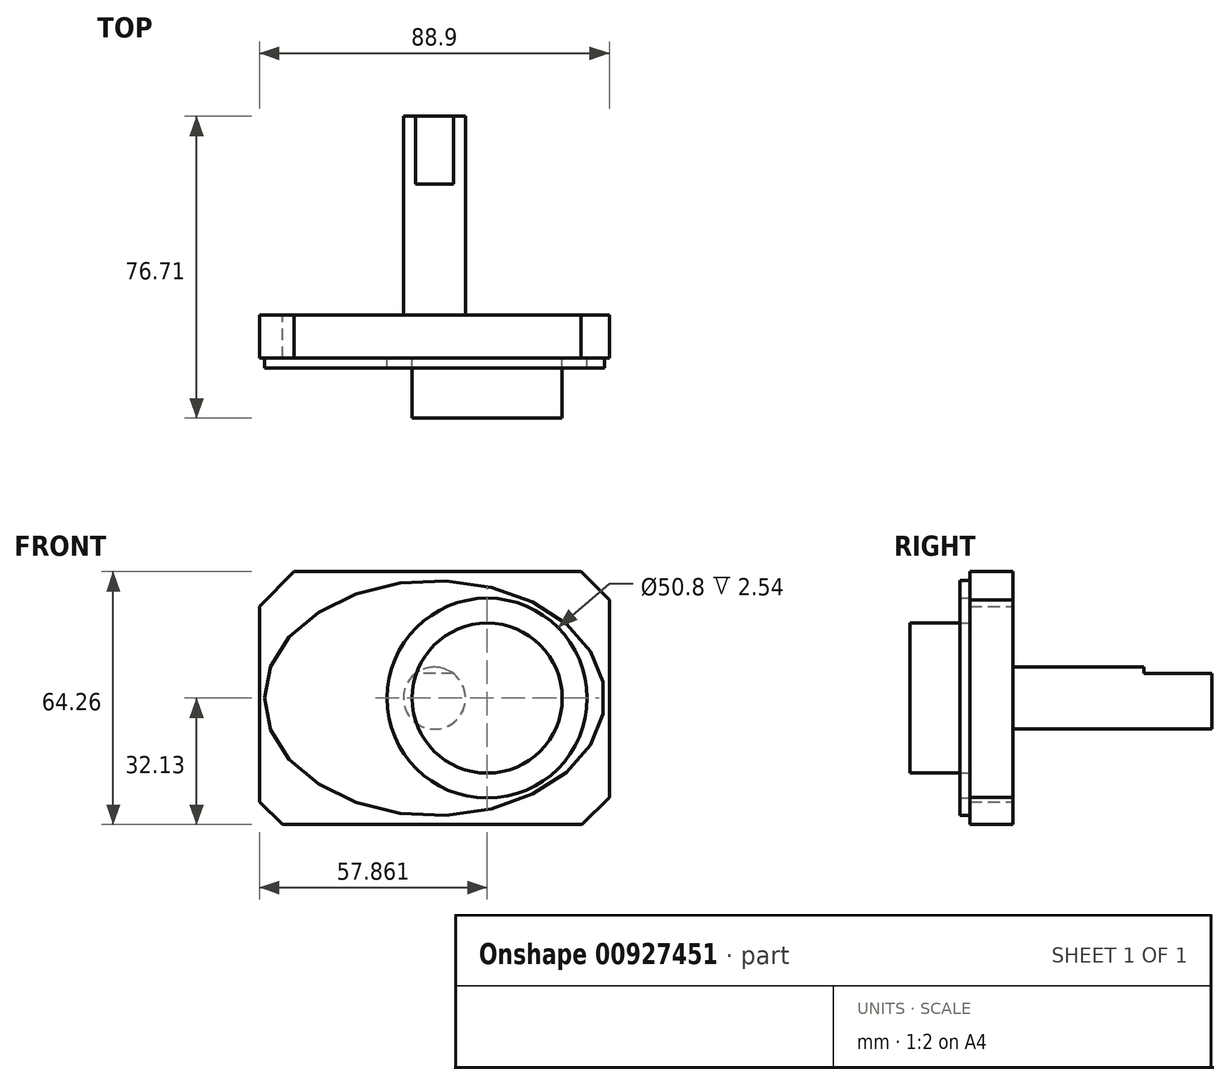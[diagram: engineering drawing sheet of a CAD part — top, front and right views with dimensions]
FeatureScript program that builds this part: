
annotation { "Feature Type Name" : "Feature", "Feature Type Description" : "" }
export const myFeature = defineFeature(function(context is Context, id is Id, definition is map)
    precondition{}
    {
        {
            var Q0;
            Q0=qCreatedBy(makeId("Front.planeOp"),FACE);
            var sketch = newSketch(context, id + "F0", { "sketchPlane" : qUnion([Q0])});
            skLineSegment(sketch, "E0.bottom", {"start": v(-44.45, -32.13) * mm, "end": v(44.45, -32.13) * mm});
            skLineSegment(sketch, "E0.top", {"start": v(-44.45, 32.13) * mm, "end": v(44.45, 32.13) * mm});
            skLineSegment(sketch, "E0.left", {"start": v(-44.45, -32.13) * mm, "end": v(-44.45, 32.13) * mm});
            skLineSegment(sketch, "E0.right", {"start": v(44.45, -32.13) * mm, "end": v(44.45, 32.13) * mm});
            skLineSegment(sketch, "E1", {"start": v(-44.45, 23.33) * mm, "end": v(-35.65, 32.13) * mm});
            skLineSegment(sketch, "E2", {"start": v(37.25, 32.13) * mm, "end": v(44.45, 24.93) * mm});
            skLineSegment(sketch, "E3", {"start": v(44.45, -25.16) * mm, "end": v(37.48, -32.13) * mm});
            skLineSegment(sketch, "E4", {"start": v(-44.45, -26.31) * mm, "end": v(-38.63, -32.13) * mm});
            skSolve(sketch);
        }
        {
            var Q0;
            {var subQ3=sQuery(id+"F0.wireOp",EDGE,"E1");Q0=makeQuery(id+"F0.imprint","IMPRINT",FACE,{"disambiguationData":[TD([[makeQuery(id+"F0.imprint","IMPRINT",EDGE,{"derivedFrom":subQ3}),-1.0]])]});}
            extrude(context, id + "F1", {"entities" : qUnion([Q0]), "depth" : 10.92 * mm, "offsetDistance" : 25.4 * mm});
        }
        {
            var Q0;
            Q0=makeQuery(id+"F1.opExtrude","CAP_FACE",FACE,{"disambiguationData":[OSD([sQuery(id+"F0.wireOp",EDGE,"E0.bottom"),sQuery(id+"F0.wireOp",EDGE,"E0.top"),sQuery(id+"F0.wireOp",EDGE,"E0.left"),sQuery(id+"F0.wireOp",EDGE,"E0.right"),sQuery(id+"F0.wireOp",EDGE,"E1"),sQuery(id+"F0.wireOp",EDGE,"E2"),sQuery(id+"F0.wireOp",EDGE,"E3"),sQuery(id+"F0.wireOp",EDGE,"E4")])],"isStart":false});
            var sketch = newSketch(context, id + "F2", { "sketchPlane" : qUnion([Q0])});
            skEllipse(sketch, "E5", {"center": v(0, 0) * mm, "majorRadius": 29.85 * mm, "minorRadius": 43.18 * mm, "majorAxis": v(0, 1)});
            skCircle(sketch, "E6", {"center": v(13.41, 0) * mm, "radius": 25.4 * mm});
            skSolve(sketch);
        }
        {
            var Q0;
            Q0=makeQuery(id+"F2.imprint","IMPRINT",FACE,{"disambiguationData":[TD([[makeQuery(id+"F2.imprint","IMPRINT",EDGE,{"derivedFrom":sQuery(id+"F2.wireOp",EDGE,"E5")}),1.0]])]});
            extrude(context, id + "F3", {"entities" : qUnion([Q0]), "operationType" : NewBodyOperationType.ADD, "depth" : 2.54 * mm, "offsetDistance" : 25.4 * mm});
        }
        {
            var Q0;
            Q0=makeQuery(id+"F3.boolean.opBoolean","SPLIT",FACE,{"disambiguationData":[TD([makeQuery(id+"F3.opExtrude","SWEPT_FACE",FACE,{"disambiguationData":[OSD([sQuery(id+"F2.wireOp",EDGE,"E6")])]})])],"derivedFrom":makeQuery(id+"F1.opExtrude","CAP_FACE",FACE,{"disambiguationData":[OSD([sQuery(id+"F0.wireOp",EDGE,"E0.bottom"),sQuery(id+"F0.wireOp",EDGE,"E0.top"),sQuery(id+"F0.wireOp",EDGE,"E0.left"),sQuery(id+"F0.wireOp",EDGE,"E0.right"),sQuery(id+"F0.wireOp",EDGE,"E1"),sQuery(id+"F0.wireOp",EDGE,"E2"),sQuery(id+"F0.wireOp",EDGE,"E3"),sQuery(id+"F0.wireOp",EDGE,"E4")])],"isStart":false})});
            var sketch = newSketch(context, id + "F4", { "sketchPlane" : qUnion([Q0])});
            skCircle(sketch, "E7", {"center": v(13.41, 0) * mm, "radius": 19.05 * mm});
            skSolve(sketch);
        }
        {
            var Q0;
            Q0=makeQuery(id+"F4.imprint","IMPRINT",FACE,{"disambiguationData":[TD([[makeQuery(id+"F4.imprint","IMPRINT",EDGE,{"derivedFrom":sQuery(id+"F4.wireOp",EDGE,"E7")}),1.0]])]});
            extrude(context, id + "F5", {"entities" : qUnion([Q0]), "operationType" : NewBodyOperationType.ADD, "depth" : 15.24 * mm, "offsetDistance" : 25.4 * mm});
        }
        {
            var Q0;
            Q0=makeQuery(id+"F1.opExtrude","CAP_FACE",FACE,{"disambiguationData":[OSD([sQuery(id+"F0.wireOp",EDGE,"E0.bottom"),sQuery(id+"F0.wireOp",EDGE,"E0.top"),sQuery(id+"F0.wireOp",EDGE,"E0.left"),sQuery(id+"F0.wireOp",EDGE,"E0.right"),sQuery(id+"F0.wireOp",EDGE,"E1"),sQuery(id+"F0.wireOp",EDGE,"E2"),sQuery(id+"F0.wireOp",EDGE,"E3"),sQuery(id+"F0.wireOp",EDGE,"E4")])],"isStart":true});
            var sketch = newSketch(context, id + "F6", { "sketchPlane" : qUnion([Q0])});
            skCircle(sketch, "E8", {"center": v(0, 0) * mm, "radius": 7.87 * mm});
            skSolve(sketch);
        }
        {
            var Q0;
            Q0=makeQuery(id+"F6.imprint","IMPRINT",FACE,{"disambiguationData":[TD([[makeQuery(id+"F6.imprint","IMPRINT",EDGE,{"derivedFrom":sQuery(id+"F6.wireOp",EDGE,"E8")}),1.0]])]});
            extrude(context, id + "F7", {"entities" : qUnion([Q0]), "operationType" : NewBodyOperationType.ADD, "depth" : 33.27 * mm, "offsetDistance" : 25.4 * mm});
        }
        {
            var Q0;
            Q0=makeQuery(id+"F7.opExtrude","CAP_FACE",FACE,{"disambiguationData":[OSD([sQuery(id+"F6.wireOp",EDGE,"E8")])],"isStart":false});
            var sketch = newSketch(context, id + "F8", { "sketchPlane" : qUnion([Q0])});
            skLineSegment(sketch, "E9", {"start": v(-4.83, 6.22) * mm, "end": v(4.83, 6.22) * mm});
            skSolve(sketch);
        }
        {
            var Q0;
            Q0 = qSketchRegion(id + "F8", true);
            var Q1;
            {var subQ0=sQuery(id+"F8.wireOp",EDGE,"E9");Q1=makeQuery(id+"F8.imprint","IMPRINT",FACE,{"disambiguationData":[TD([[makeQuery(id+"F8.imprint","IMPRINT",EDGE,{"derivedFrom":subQ0}),-1.0]])]});}
            extrude(context, id + "F9", {"entities" : qUnion([Q0, Q1]), "operationType" : NewBodyOperationType.ADD, "depth" : 17.27 * mm, "offsetDistance" : 25.4 * mm});
        }
    });
